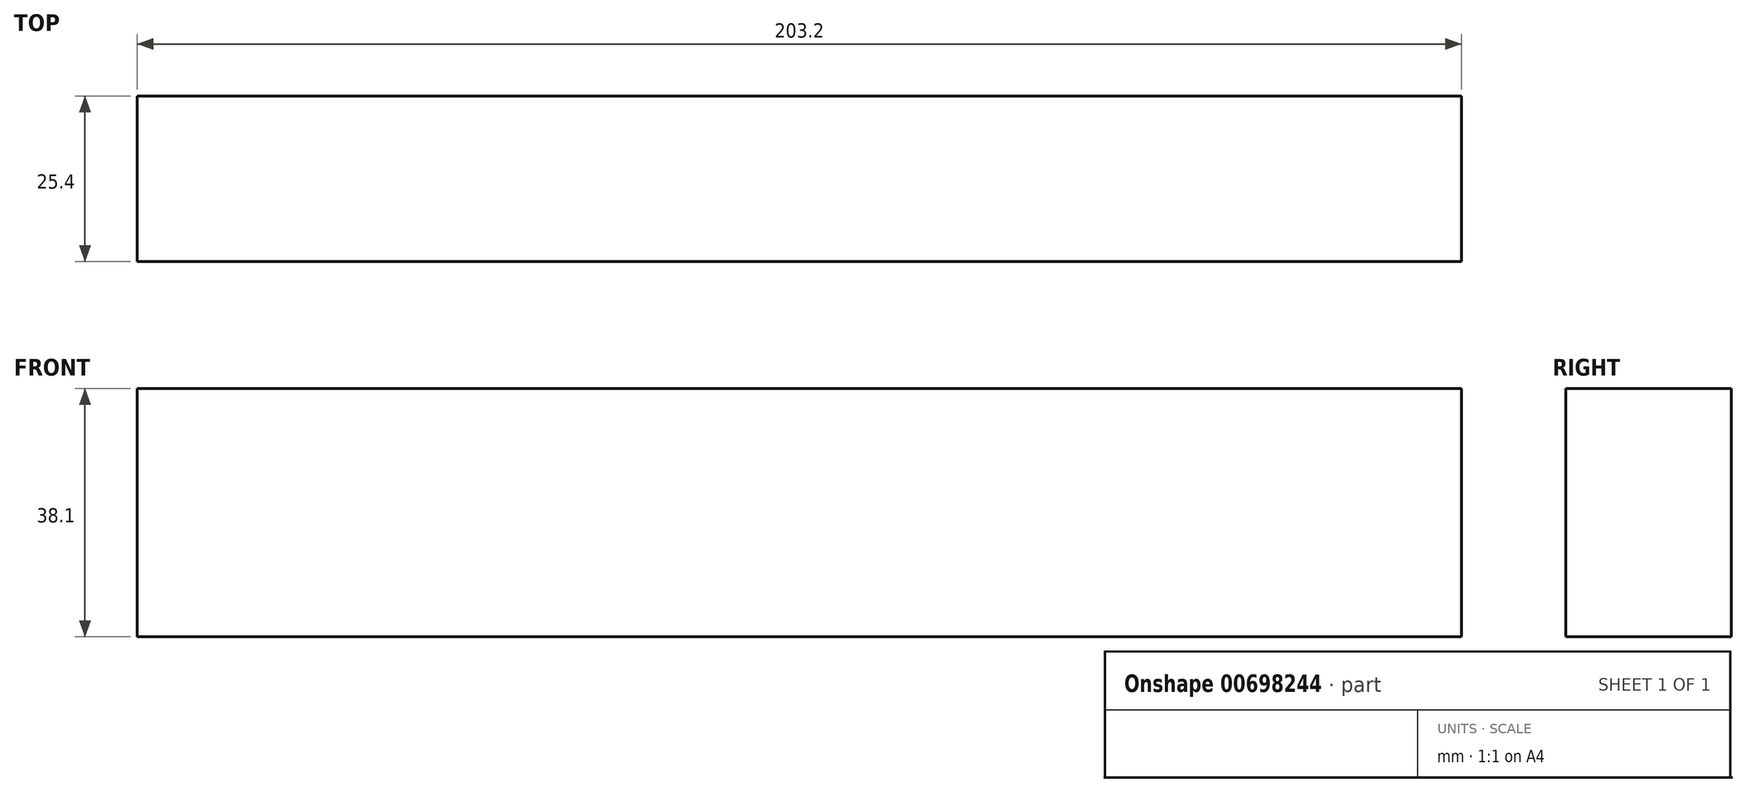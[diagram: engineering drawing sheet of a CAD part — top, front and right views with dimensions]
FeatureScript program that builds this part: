
annotation { "Feature Type Name" : "Feature", "Feature Type Description" : "" }
export const myFeature = defineFeature(function(context is Context, id is Id, definition is map)
    precondition{}
    {
        {
            var Q0;
            Q0=qCreatedBy(makeId("Front.planeOp"),FACE);
            var sketch = newSketch(context, id + "F0", { "sketchPlane" : qUnion([Q0])});
            skLineSegment(sketch, "E0.bottom", {"start": v(-128.53, -5.04) * mm, "end": v(74.67, -5.04) * mm});
            skLineSegment(sketch, "E0.top", {"start": v(-128.53, -43.14) * mm, "end": v(74.67, -43.14) * mm});
            skLineSegment(sketch, "E0.left", {"start": v(-128.53, -5.04) * mm, "end": v(-128.53, -43.14) * mm});
            skLineSegment(sketch, "E0.right", {"start": v(74.67, -5.04) * mm, "end": v(74.67, -43.14) * mm});
            skSolve(sketch);
        }
        {
            var Q0;
            Q0 = qSketchRegion(id + "F0", true);
            extrude(context, id + "F1", {"entities" : qUnion([Q0]), "depth" : 25.4 * mm, "offsetDistance" : 25.4 * mm});
        }
    });
